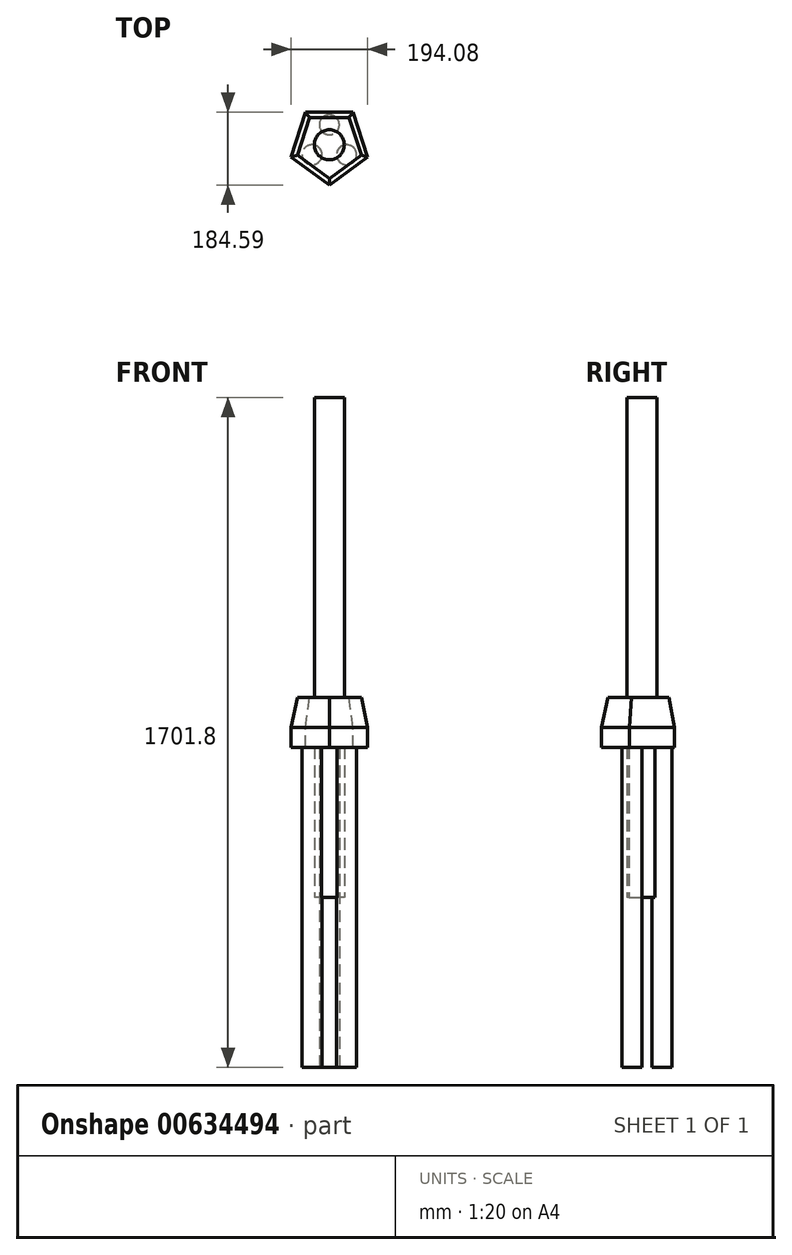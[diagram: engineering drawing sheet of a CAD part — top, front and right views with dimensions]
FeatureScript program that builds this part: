
annotation { "Feature Type Name" : "Feature", "Feature Type Description" : "" }
export const myFeature = defineFeature(function(context is Context, id is Id, definition is map)
    precondition{}
    {
        {
            var Q0;
            Q0=qCreatedBy(makeId("Top.planeOp"),FACE);
            var sketch = newSketch(context, id + "F0", { "sketchPlane" : qUnion([Q0])});
            skCircle(sketch, "E0", {"center": v(0, 50.8) * mm, "radius": 25.4 * mm});
            skCircle(sketch, "E1.1.0", {"center": v(-44, -25.4) * mm, "radius": 25.4 * mm});
            skCircle(sketch, "E1.2.0", {"center": v(44, -25.4) * mm, "radius": 25.4 * mm});
            skPoint(sketch, "E1.center", {"position": v(0, 0) * mm});
            skCircle(sketch, "E2", {"center": v(0, 0) * mm, "radius": 50.8 * mm, "construction": true});
            skSolve(sketch);
        }
        {
            var Q0;
            Q0 = qSketchRegion(id + "F0", true);
            extrude(context, id + "F1", {"entities" : qUnion([Q0]), "depth" : 863.6 * mm, "offsetDistance" : 25.4 * mm});
        }
        {
            var Q0;
            Q0=makeQuery(id+"F1.opExtrude","CAP_FACE",FACE,{"disambiguationData":[OSD([sQuery(id+"F0.wireOp",EDGE,"E1.1.0")])],"isStart":false});
            var sketch = newSketch(context, id + "F2", { "sketchPlane" : qUnion([Q0])});
            skCircle(sketch, "E3.cCircle", {"center": v(0, 0) * mm, "radius": 82.55 * mm, "construction": true});
            skLineSegment(sketch, "E3.0", {"start": v(-59.98, 82.55) * mm, "end": v(59.98, 82.55) * mm});
            skLineSegment(sketch, "E3.1", {"start": v(59.98, 82.55) * mm, "end": v(97.04, -31.53) * mm});
            skLineSegment(sketch, "E3.2", {"start": v(97.04, -31.53) * mm, "end": v(0, -102.04) * mm});
            skLineSegment(sketch, "E3.3", {"start": v(0, -102.04) * mm, "end": v(-97.04, -31.53) * mm});
            skLineSegment(sketch, "E3.4", {"start": v(-97.04, -31.53) * mm, "end": v(-59.98, 82.55) * mm});
            skPoint(sketch, "E3.0.midPoint", {"position": v(0, 82.55) * mm});
            skSolve(sketch);
        }
        {
            var Q0;
            Q0=makeQuery(id+"F2.imprint","IMPRINT",FACE,{"disambiguationData":[TD([[makeQuery(id+"F2.imprint","IMPRINT",EDGE,{"derivedFrom":sQuery(id+"F2.wireOp",EDGE,"E3.0")}),-1.0]])]});
            var Q1;
            Q1=makeQuery(id+"F2.imprint","IMPRINT",FACE,{"disambiguationData":[TD([[makeQuery(id+"F2.imprint","IMPRINT",EDGE,{"derivedFrom":makeQuery(id+"F1.opExtrude","CAP_EDGE",EDGE,{"disambiguationData":[OSD([sQuery(id+"F0.wireOp",EDGE,"E1.1.0")])],"isStart":false})}),1.0]])]});
            extrude(context, id + "F3", {"entities" : qUnion([Q0, Q1]), "operationType" : NewBodyOperationType.ADD, "oppositeDirection" : true, "depth" : 50.8 * mm, "offsetDistance" : 25.4 * mm, "hasSecondDirection" : true, "secondDirectionOppositeDirection" : false, "secondDirectionDepth" : 76.2 * mm, "hasSecondDirectionDraft" : true, "secondDirectionDraftAngle" : 10 * degree, "secondDirectionDraftPullDirection" : true});
        }
        {
            var Q0;
            Q0=makeQuery(id+"F3.opExtrude","CAP_FACE",FACE,{"disambiguationData":[OSD([sQuery(id+"F2.wireOp",EDGE,"E3.0"),sQuery(id+"F2.wireOp",EDGE,"E3.1"),sQuery(id+"F2.wireOp",EDGE,"E3.2"),sQuery(id+"F2.wireOp",EDGE,"E3.3"),sQuery(id+"F2.wireOp",EDGE,"E3.4")])],"isStart":true});
            var sketch = newSketch(context, id + "F4", { "sketchPlane" : qUnion([Q0])});
            skCircle(sketch, "E4", {"center": v(0, 0) * mm, "radius": 38.1 * mm});
            skSolve(sketch);
        }
        {
            var Q0;
            Q0=makeQuery(id+"F4.imprint","IMPRINT",FACE,{"disambiguationData":[TD([[makeQuery(id+"F4.imprint","IMPRINT",EDGE,{"derivedFrom":sQuery(id+"F4.wireOp",EDGE,"E4")}),1.0]])]});
            var Q1;
            Q1=sQuery(id+"F4.wireOp",EDGE,"E4");
            extrude(context, id + "F5", {"entities" : qUnion([Q0]), "operationType" : NewBodyOperationType.ADD, "surfaceEntities" : qUnion([Q1]), "depth" : 762 * mm, "offsetDistance" : 25.4 * mm, "hasSecondDirection" : true, "secondDirectionOppositeDirection" : true, "secondDirectionDepth" : 508 * mm});
        }
    });
